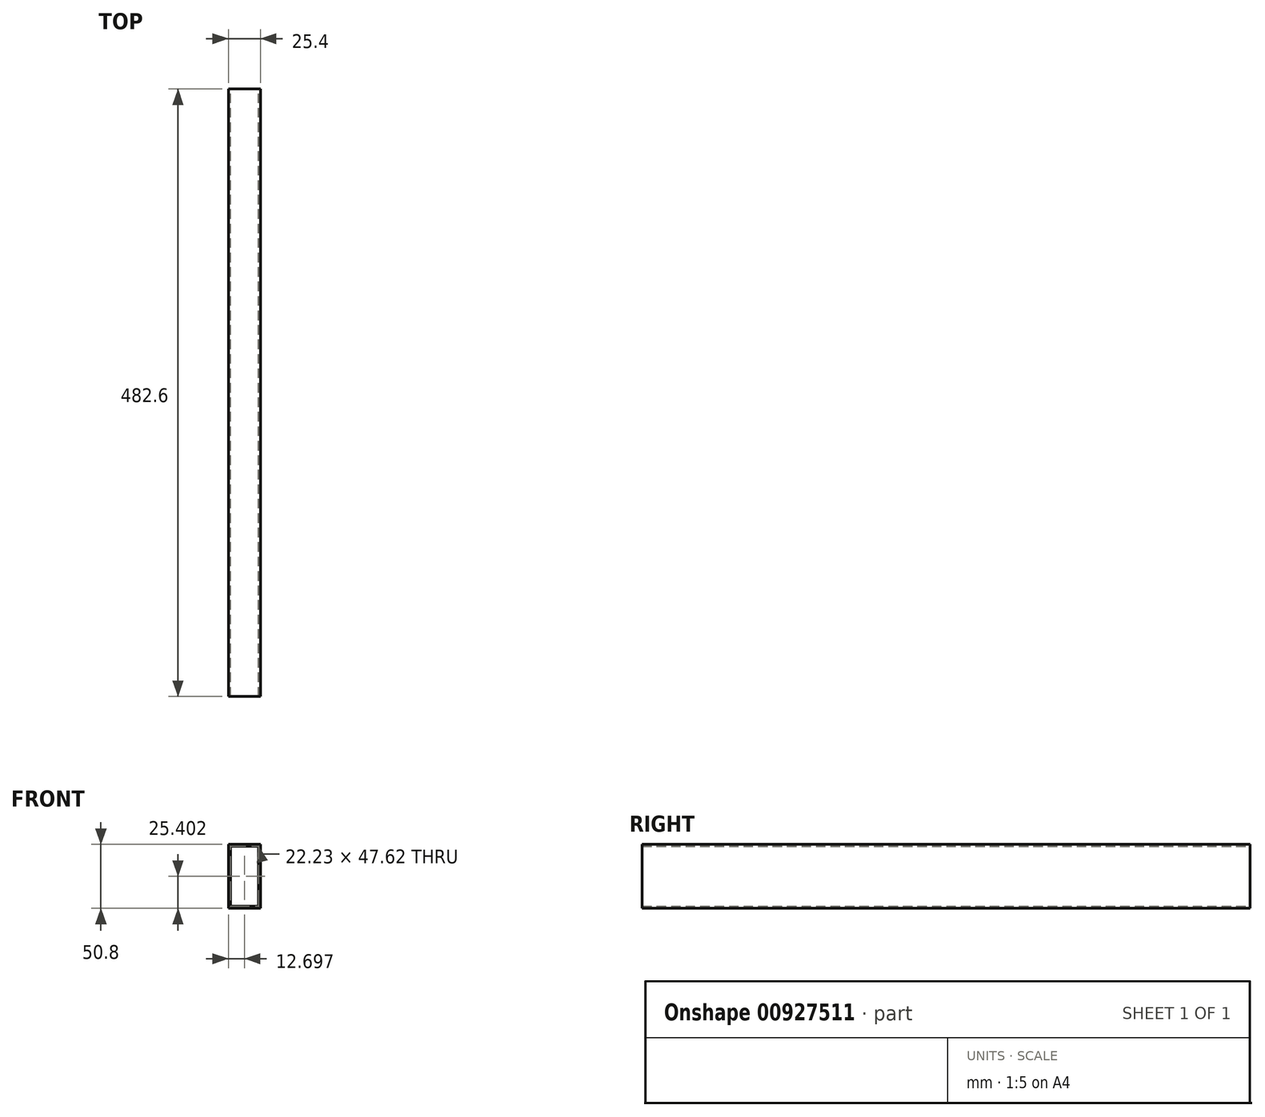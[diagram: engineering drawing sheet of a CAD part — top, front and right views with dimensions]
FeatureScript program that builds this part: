
annotation { "Feature Type Name" : "Feature", "Feature Type Description" : "" }
export const myFeature = defineFeature(function(context is Context, id is Id, definition is map)
    precondition{}
    {
        {
            var Q0;
            Q0=qCreatedBy(makeId("Front.planeOp"),FACE);
            var sketch = newSketch(context, id + "F0", { "sketchPlane" : qUnion([Q0])});
            skLineSegment(sketch, "E0.bottom", {"start": v(-1.76, 50.13) * mm, "end": v(23.64, 50.13) * mm});
            skLineSegment(sketch, "E0.top", {"start": v(-1.76, -0.67) * mm, "end": v(23.64, -0.67) * mm});
            skLineSegment(sketch, "E0.left", {"start": v(-1.76, 50.13) * mm, "end": v(-1.76, -0.67) * mm});
            skLineSegment(sketch, "E0.right", {"start": v(23.64, 50.13) * mm, "end": v(23.64, -0.67) * mm});
            skLineSegment(sketch, "E1.bottom", {"start": v(-0.18, 48.54) * mm, "end": v(22.05, 48.54) * mm});
            skLineSegment(sketch, "E1.top", {"start": v(-0.18, 0.92) * mm, "end": v(22.05, 0.92) * mm});
            skLineSegment(sketch, "E1.left", {"start": v(-0.18, 48.54) * mm, "end": v(-0.18, 0.92) * mm});
            skLineSegment(sketch, "E1.right", {"start": v(22.05, 48.54) * mm, "end": v(22.05, 0.92) * mm});
            skSolve(sketch);
        }
        {
            var Q0;
            Q0=makeQuery(id+"F0.imprint","IMPRINT",FACE,{"disambiguationData":[TD([[makeQuery(id+"F0.imprint","IMPRINT",EDGE,{"derivedFrom":sQuery(id+"F0.wireOp",EDGE,"E0.bottom")}),-1.0]])]});
            extrude(context, id + "F1", {"entities" : qUnion([Q0]), "depth" : 482.6 * mm, "offsetDistance" : 25.4 * mm});
        }
    });
